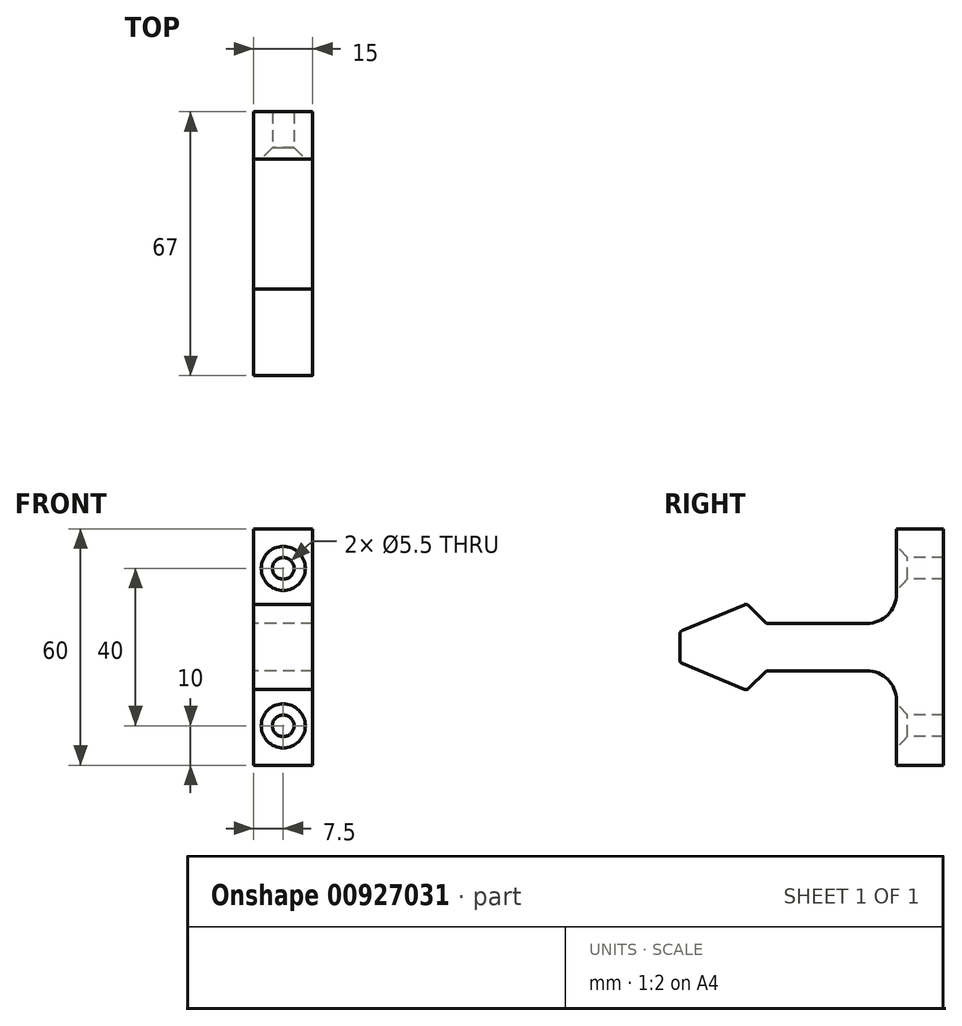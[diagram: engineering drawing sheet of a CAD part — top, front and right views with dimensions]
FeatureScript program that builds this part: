
annotation { "Feature Type Name" : "Feature", "Feature Type Description" : "" }
export const myFeature = defineFeature(function(context is Context, id is Id, definition is map)
    precondition{}
    {
        {
            var Q0;
            Q0=qCreatedBy(makeId("Right.planeOp"),FACE);
            var sketch = newSketch(context, id + "F0", { "sketchPlane" : qUnion([Q0])});
            skLineSegment(sketch, "E0.bottom", {"start": v(0, 30) * mm, "end": v(-12, 30) * mm});
            skLineSegment(sketch, "E0.top", {"start": v(0, -30) * mm, "end": v(-12, -30) * mm});
            skLineSegment(sketch, "E0.left", {"start": v(0, 30) * mm, "end": v(0, -30) * mm});
            skLineSegment(sketch, "E0.right", {"start": v(-12, 30) * mm, "end": v(-12, -30) * mm});
            skLineSegment(sketch, "E1.bottom", {"start": v(-12, 6) * mm, "end": v(-62, 6) * mm});
            skLineSegment(sketch, "E1.top", {"start": v(-12, -6) * mm, "end": v(-62, -6) * mm});
            skLineSegment(sketch, "E1.left", {"start": v(-12, 6) * mm, "end": v(-12, -6) * mm});
            skLineSegment(sketch, "E1.right", {"start": v(-62, 6) * mm, "end": v(-62, -6) * mm});
            skLineSegment(sketch, "E2", {"start": v(-45, 6) * mm, "end": v(-50, 11) * mm});
            skLineSegment(sketch, "E3", {"start": v(-50, 11) * mm, "end": v(-67, 3.92) * mm});
            skLineSegment(sketch, "E4", {"start": v(-67, 3.92) * mm, "end": v(-67, 0) * mm});
            skLineSegment(sketch, "E5", {"start": v(0, 0) * mm, "end": v(-67, 0) * mm});
            skLineSegment(sketch, "E6.MirrorCS", {"start": v(-67, -3.92) * mm, "end": v(-67, 0) * mm});
            skLineSegment(sketch, "E7.MirrorCS", {"start": v(-50, -11) * mm, "end": v(-67, -3.92) * mm});
            skLineSegment(sketch, "E8.MirrorCS", {"start": v(-45, -6) * mm, "end": v(-50, -11) * mm});
            skSolve(sketch);
        }
        {
            var Q0;
            {var subQ5=sQuery(id+"F0.wireOp",EDGE,"E4");Q0=makeQuery(id+"F0.imprint","IMPRINT",FACE,{"disambiguationData":[TD([[makeQuery(id+"F0.imprint","IMPRINT",EDGE,{"derivedFrom":subQ5}),1.0]])]});}
            var Q1;
            {var subQ3=sQuery(id+"F0.wireOp",EDGE,"E2");Q1=makeQuery(id+"F0.imprint","IMPRINT",FACE,{"disambiguationData":[TD([[makeQuery(id+"F0.imprint","IMPRINT",EDGE,{"derivedFrom":subQ3}),1.0]])]});}
            var Q2;
            {var subQ1=sQuery(id+"F0.wireOp",EDGE,"E1.bottom");var subQ6=sQuery(id+"F0.wireOp",EDGE,"E0.right");var subQ7=makeQuery(id+"F0.imprint","INTERSECT",VERTEX,{"derivedFrom":[subQ6,subQ1]});Q2=makeQuery(id+"F0.imprint","IMPRINT",FACE,{"disambiguationData":[TD([[makeQuery(id+"F0.imprint","IMPRINT",EDGE,{"disambiguationData":[TD([[subQ7,-1.0]])],"derivedFrom":subQ6}),-1.0]])]});}
            var Q3;
            {var subQ5=sQuery(id+"F0.wireOp",EDGE,"E6.MirrorCS");Q3=makeQuery(id+"F0.imprint","IMPRINT",FACE,{"disambiguationData":[TD([[makeQuery(id+"F0.imprint","IMPRINT",EDGE,{"derivedFrom":subQ5}),-1.0]])]});}
            var Q4;
            {var subQ3=sQuery(id+"F0.wireOp",EDGE,"E8.MirrorCS");Q4=makeQuery(id+"F0.imprint","IMPRINT",FACE,{"disambiguationData":[TD([[makeQuery(id+"F0.imprint","IMPRINT",EDGE,{"derivedFrom":subQ3}),-1.0]])]});}
            var Q5;
            {var subQ1=sQuery(id+"F0.wireOp",EDGE,"E1.top");var subQ4=sQuery(id+"F0.wireOp",EDGE,"E0.right");var subQ5=makeQuery(id+"F0.imprint","INTERSECT",VERTEX,{"derivedFrom":[subQ4,subQ1]});Q5=makeQuery(id+"F0.imprint","IMPRINT",FACE,{"disambiguationData":[TD([[makeQuery(id+"F0.imprint","IMPRINT",EDGE,{"disambiguationData":[TD([[subQ5,1.0]])],"derivedFrom":subQ4}),-1.0]])]});}
            var Q6;
            {var subQ5=sQuery(id+"F0.wireOp",EDGE,"E0.bottom");Q6=makeQuery(id+"F0.imprint","IMPRINT",FACE,{"disambiguationData":[TD([[makeQuery(id+"F0.imprint","IMPRINT",EDGE,{"derivedFrom":subQ5}),1.0]])]});}
            var Q7;
            {var subQ4=sQuery(id+"F0.wireOp",EDGE,"E0.top");Q7=makeQuery(id+"F0.imprint","IMPRINT",FACE,{"disambiguationData":[TD([[makeQuery(id+"F0.imprint","IMPRINT",EDGE,{"derivedFrom":subQ4}),-1.0]])]});}
            extrude(context, id + "F1", {"entities" : qUnion([Q0, Q1, Q2, Q3, Q4, Q5, Q6, Q7]), "endBound" : BoundingType.SYMMETRIC, "depth" : 15 * mm, "offsetDistance" : 25 * mm});
        }
        {
            var Q0;
            Q0=makeQuery(id+"F1.opExtrude","SWEPT_EDGE",EDGE,{"disambiguationData":[OSD([sQuery(id+"F0.wireOp",EDGE,"E2"),sQuery(id+"F0.wireOp",EDGE,"E3")])]});
            var Q1;
            Q1=makeQuery(id+"F1.opExtrude","SWEPT_EDGE",EDGE,{"disambiguationData":[OSD([sQuery(id+"F0.wireOp",EDGE,"E3"),sQuery(id+"F0.wireOp",EDGE,"E4")])]});
            var Q2;
            Q2=makeQuery(id+"F1.opExtrude","SWEPT_EDGE",EDGE,{"disambiguationData":[OSD([sQuery(id+"F0.wireOp",EDGE,"E6.MirrorCS"),sQuery(id+"F0.wireOp",EDGE,"E7.MirrorCS")])]});
            var Q3;
            Q3=makeQuery(id+"F1.opExtrude","SWEPT_EDGE",EDGE,{"disambiguationData":[OSD([sQuery(id+"F0.wireOp",EDGE,"E7.MirrorCS"),sQuery(id+"F0.wireOp",EDGE,"E8.MirrorCS")])]});
            fillet(context, id + "F2", {"entities" : qUnion([Q0, Q1, Q2, Q3]), "radius" : 1 * mm, "tangentPropagation" : true, "allowEdgeOverflow" : false});
        }
        {
            var Q0;
            {var subQ0=sQuery(id+"F0.wireOp",EDGE,"E0.right");Q0=makeQuery(id+"F1.opExtrude","SWEPT_FACE",FACE,{"disambiguationData":[OSD([subQ0]),TDD([makeQuery(id+"F0.imprint","IMPRINT",EDGE,{"disambiguationData":[TD([[makeQuery(id+"F0.imprint","INTERSECT",VERTEX,{"derivedFrom":[sQuery(id+"F0.wireOp",EDGE,"E0.bottom"),subQ0]}),-1.0]])],"derivedFrom":subQ0})])]});}
            var sketch = newSketch(context, id + "F3", { "sketchPlane" : qUnion([Q0])});
            skPoint(sketch, "E9", {"position": v(0, 20) * mm});
            skPoint(sketch, "E10", {"position": v(0, -20) * mm});
            skSolve(sketch);
        }
        {
            var Q0;
            Q0=sQuery(id+"F3.wireOp",VERTEX,"E9");
            var Q1;
            Q1=sQuery(id+"F3.wireOp",VERTEX,"E10");
            var Q2;
            Q2=makeQuery(id+"F1.opExtrude","SWEPT_BODY",BODY,{"disambiguationData":[OSD([sQuery(id+"F0.wireOp",EDGE,"E0.bottom"),sQuery(id+"F0.wireOp",EDGE,"E0.top"),sQuery(id+"F0.wireOp",EDGE,"E0.left"),sQuery(id+"F0.wireOp",EDGE,"E0.right"),sQuery(id+"F0.wireOp",EDGE,"E1.bottom"),sQuery(id+"F0.wireOp",EDGE,"E1.top"),sQuery(id+"F0.wireOp",EDGE,"E2"),sQuery(id+"F0.wireOp",EDGE,"E3"),sQuery(id+"F0.wireOp",EDGE,"E4"),sQuery(id+"F0.wireOp",EDGE,"E6.MirrorCS"),sQuery(id+"F0.wireOp",EDGE,"E7.MirrorCS"),sQuery(id+"F0.wireOp",EDGE,"E8.MirrorCS")])]});
            hole(context, id + "F4", {"style" : HoleStyle.C_SINK, "endStyle" : HoleEndStyle.THROUGH, "standardTappedOrClearance" : lookupTablePath({ "fit" : "Normal", "standard" : "ISO", "size" : "M5", "type" : "Clearance" }), "standardBlindInLast" : lookupTablePath({ "fit" : "Normal", "standard" : "ISO", "size" : "M5", "type" : "Clearance" }), "holeDiameter" : 5.5 * mm, "cSinkDiameter" : 11.2 * mm, "cSinkAngle" : 90 * degree, "majorDiameter" : 5 * mm, "isTappedThrough" : true, "tappedDepth" : 12 * mm, "tapClearance" : 3, "locations" : qUnion([Q0, Q1]), "scope" : qUnion([Q2])});
        }
        {
            var Q0;
            Q0=makeQuery(id+"F1.opExtrude","SWEPT_EDGE",EDGE,{"disambiguationData":[OSD([sQuery(id+"F0.wireOp",EDGE,"E0.right"),sQuery(id+"F0.wireOp",EDGE,"E1.bottom")])]});
            var Q1;
            Q1=makeQuery(id+"F1.opExtrude","SWEPT_EDGE",EDGE,{"disambiguationData":[OSD([sQuery(id+"F0.wireOp",EDGE,"E0.right"),sQuery(id+"F0.wireOp",EDGE,"E1.top")])]});
            fillet(context, id + "F5", {"entities" : qUnion([Q0, Q1]), "radius" : 7.5 * mm, "tangentPropagation" : true, "allowEdgeOverflow" : false});
        }
    });
